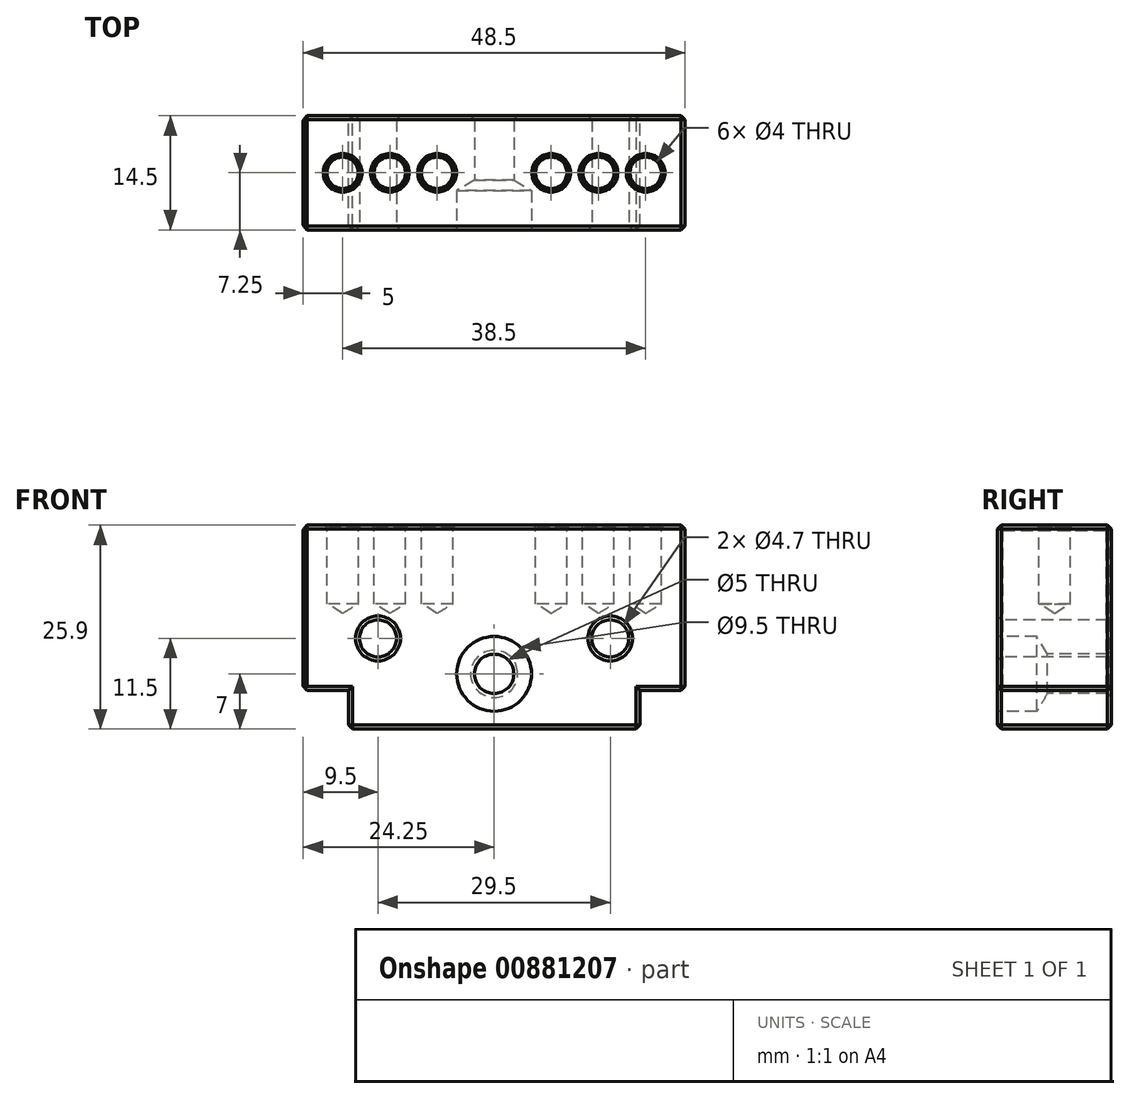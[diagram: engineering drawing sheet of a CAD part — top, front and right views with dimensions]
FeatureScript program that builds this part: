
annotation { "Feature Type Name" : "Feature", "Feature Type Description" : "" }
export const myFeature = defineFeature(function(context is Context, id is Id, definition is map)
    precondition{}
    {
        {
            var Q0;
            Q0=qCreatedBy(makeId("Front.planeOp"),FACE);
            var sketch = newSketch(context, id + "F0", { "sketchPlane" : qUnion([Q0])});
            skLineSegment(sketch, "E0", {"start": v(0, 4.9) * mm, "end": v(5.75, 4.9) * mm});
            skLineSegment(sketch, "E1", {"start": v(5.75, 4.9) * mm, "end": v(5.75, 0) * mm});
            skLineSegment(sketch, "E2", {"start": v(5.75, 0) * mm, "end": v(42.75, 0) * mm});
            skLineSegment(sketch, "E3", {"start": v(42.75, 0) * mm, "end": v(42.75, 4.9) * mm});
            skLineSegment(sketch, "E4", {"start": v(42.75, 4.9) * mm, "end": v(48.5, 4.9) * mm});
            skLineSegment(sketch, "E5", {"start": v(48.5, 4.9) * mm, "end": v(48.5, 25.9) * mm});
            skLineSegment(sketch, "E6", {"start": v(48.5, 25.9) * mm, "end": v(0, 25.9) * mm});
            skLineSegment(sketch, "E7", {"start": v(0, 25.9) * mm, "end": v(0, 4.9) * mm});
            skSolve(sketch);
        }
        {
            var Q0;
            Q0=makeQuery(id+"F0.imprint","IMPRINT",FACE,{"disambiguationData":[TD([[makeQuery(id+"F0.imprint","IMPRINT",EDGE,{"derivedFrom":sQuery(id+"F0.wireOp",EDGE,"E0")}),1.0]])]});
            extrude(context, id + "F1", {"entities" : qUnion([Q0]), "depth" : 14.5 * mm, "offsetDistance" : 25 * mm});
        }
        {
            var Q0;
            Q0=makeQuery(id+"F1.opExtrude","CAP_FACE",FACE,{"disambiguationData":[OSD([sQuery(id+"F0.wireOp",EDGE,"E0"),sQuery(id+"F0.wireOp",EDGE,"E1"),sQuery(id+"F0.wireOp",EDGE,"E2"),sQuery(id+"F0.wireOp",EDGE,"E3"),sQuery(id+"F0.wireOp",EDGE,"E4"),sQuery(id+"F0.wireOp",EDGE,"E5"),sQuery(id+"F0.wireOp",EDGE,"E6"),sQuery(id+"F0.wireOp",EDGE,"E7")])],"isStart":false});
            var sketch = newSketch(context, id + "F2", { "sketchPlane" : qUnion([Q0])});
            skPoint(sketch, "E8", {"position": v(24.25, 7) * mm});
            skPoint(sketch, "E9", {"position": v(9.5, 11.5) * mm});
            skPoint(sketch, "E10", {"position": v(39, 11.5) * mm});
            skPoint(sketch, "E11.end.orphan", {"position": v(0, 7) * mm});
            skSolve(sketch);
        }
        {
            var Q0;
            Q0=sQuery(id+"F2.wireOp",VERTEX,"E9");
            var Q1;
            Q1=sQuery(id+"F2.wireOp",VERTEX,"E10");
            var Q2;
            Q2=makeQuery(id+"F1.opExtrude","SWEPT_BODY",BODY,{"disambiguationData":[OSD([sQuery(id+"F0.wireOp",EDGE,"E0"),sQuery(id+"F0.wireOp",EDGE,"E1"),sQuery(id+"F0.wireOp",EDGE,"E2"),sQuery(id+"F0.wireOp",EDGE,"E3"),sQuery(id+"F0.wireOp",EDGE,"E4"),sQuery(id+"F0.wireOp",EDGE,"E5"),sQuery(id+"F0.wireOp",EDGE,"E6"),sQuery(id+"F0.wireOp",EDGE,"E7")])]});
            hole(context, id + "F3", {"style" : HoleStyle.SIMPLE, "endStyle" : HoleEndStyle.THROUGH, "holeDiameter" : 4.7 * mm, "majorDiameter" : 5 * mm, "isTappedThrough" : true, "tappedDepth" : 6 * mm, "tapClearance" : 3, "locations" : qUnion([Q0, Q1]), "scope" : qUnion([Q2])});
        }
        {
            var Q0;
            Q0=sQuery(id+"F2.wireOp",VERTEX,"E8");
            var Q1;
            Q1=makeQuery(id+"F1.opExtrude","SWEPT_BODY",BODY,{"disambiguationData":[OSD([sQuery(id+"F0.wireOp",EDGE,"E0"),sQuery(id+"F0.wireOp",EDGE,"E1"),sQuery(id+"F0.wireOp",EDGE,"E2"),sQuery(id+"F0.wireOp",EDGE,"E3"),sQuery(id+"F0.wireOp",EDGE,"E4"),sQuery(id+"F0.wireOp",EDGE,"E5"),sQuery(id+"F0.wireOp",EDGE,"E6"),sQuery(id+"F0.wireOp",EDGE,"E7")])]});
            hole(context, id + "F4", {"style" : HoleStyle.SIMPLE, "endStyle" : HoleEndStyle.THROUGH, "standardTappedOrClearance" : lookupTablePath({ "standard" : "ISO", "engagement" : "75%", "pitch" : "1 mm", "size" : "M6", "type" : "Tapped" }), "standardBlindInLast" : lookupTablePath({ "standard" : "ISO", "engagement" : "75%", "pitch" : "1 mm", "size" : "M6", "type" : "Tapped" }), "holeDiameter" : 5 * mm, "majorDiameter" : 6 * mm, "showTappedDepth" : true, "isTappedThrough" : true, "tappedDepth" : 6 * mm, "tapClearance" : 3, "locations" : qUnion([Q0]), "scope" : qUnion([Q1])});
        }
        {
            var Q0;
            Q0=makeQuery(id+"F1.opExtrude","SWEPT_FACE",FACE,{"disambiguationData":[OSD([sQuery(id+"F0.wireOp",EDGE,"E6")])]});
            var sketch = newSketch(context, id + "F5", { "sketchPlane" : qUnion([Q0])});
            skLineSegment(sketch, "E12", {"start": v(0, -7.25) * mm, "end": v(52.15, -7.25) * mm, "construction": true});
            skPoint(sketch, "E13", {"position": v(5, -7.25) * mm});
            skPoint(sketch, "E14", {"position": v(11, -7.25) * mm});
            skPoint(sketch, "E15", {"position": v(17, -7.25) * mm});
            skLineSegment(sketch, "E16", {"start": v(24.25, 0) * mm, "end": v(24.25, -16.26) * mm, "construction": true});
            skPoint(sketch, "E17.MirrorP", {"position": v(31.5, -7.25) * mm});
            skPoint(sketch, "E18.MirrorP", {"position": v(37.5, -7.25) * mm});
            skPoint(sketch, "E19.MirrorP", {"position": v(43.5, -7.25) * mm});
            skSolve(sketch);
        }
        {
            var Q0;
            Q0=sQuery(id+"F5.wireOp",VERTEX,"E13");
            var Q1;
            Q1=sQuery(id+"F5.wireOp",VERTEX,"E14");
            var Q2;
            Q2=sQuery(id+"F5.wireOp",VERTEX,"E15");
            var Q3;
            Q3=sQuery(id+"F5.wireOp",VERTEX,"E17.MirrorP");
            var Q4;
            Q4=sQuery(id+"F5.wireOp",VERTEX,"E18.MirrorP");
            var Q5;
            Q5=sQuery(id+"F5.wireOp",VERTEX,"E19.MirrorP");
            var Q6;
            Q6=makeQuery(id+"F1.opExtrude","SWEPT_BODY",BODY,{"disambiguationData":[OSD([sQuery(id+"F0.wireOp",EDGE,"E0"),sQuery(id+"F0.wireOp",EDGE,"E1"),sQuery(id+"F0.wireOp",EDGE,"E2"),sQuery(id+"F0.wireOp",EDGE,"E3"),sQuery(id+"F0.wireOp",EDGE,"E4"),sQuery(id+"F0.wireOp",EDGE,"E5"),sQuery(id+"F0.wireOp",EDGE,"E6"),sQuery(id+"F0.wireOp",EDGE,"E7")])]});
            hole(context, id + "F6", {"style" : HoleStyle.C_SINK, "endStyle" : HoleEndStyle.BLIND, "holeDiameter" : 4 * mm, "cSinkDiameter" : 4.5 * mm, "cSinkAngle" : 90 * degree, "majorDiameter" : 5 * mm, "holeDepth" : 10 * mm, "isTappedThrough" : true, "tappedDepth" : 6 * mm, "tapClearance" : 3, "locations" : qUnion([Q0, Q1, Q2, Q3, Q4, Q5]), "scope" : qUnion([Q6])});
        }
        {
            var Q0;
            Q0=makeQuery(id+"F1.opExtrude","SWEPT_FACE",FACE,{"disambiguationData":[OSD([sQuery(id+"F0.wireOp",EDGE,"E5")])]});
            var Q1;
            Q1=makeQuery(id+"F1.opExtrude","SWEPT_FACE",FACE,{"disambiguationData":[OSD([sQuery(id+"F0.wireOp",EDGE,"E6")])]});
            var Q2;
            Q2=makeQuery(id+"F1.opExtrude","CAP_FACE",FACE,{"disambiguationData":[OSD([sQuery(id+"F0.wireOp",EDGE,"E0"),sQuery(id+"F0.wireOp",EDGE,"E1"),sQuery(id+"F0.wireOp",EDGE,"E2"),sQuery(id+"F0.wireOp",EDGE,"E3"),sQuery(id+"F0.wireOp",EDGE,"E4"),sQuery(id+"F0.wireOp",EDGE,"E5"),sQuery(id+"F0.wireOp",EDGE,"E6"),sQuery(id+"F0.wireOp",EDGE,"E7")])],"isStart":false});
            var Q3;
            Q3=makeQuery(id+"F1.opExtrude","CAP_FACE",FACE,{"disambiguationData":[OSD([sQuery(id+"F0.wireOp",EDGE,"E0"),sQuery(id+"F0.wireOp",EDGE,"E1"),sQuery(id+"F0.wireOp",EDGE,"E2"),sQuery(id+"F0.wireOp",EDGE,"E3"),sQuery(id+"F0.wireOp",EDGE,"E4"),sQuery(id+"F0.wireOp",EDGE,"E5"),sQuery(id+"F0.wireOp",EDGE,"E6"),sQuery(id+"F0.wireOp",EDGE,"E7")])],"isStart":true});
            var Q4;
            Q4=makeQuery(id+"F1.opExtrude","SWEPT_FACE",FACE,{"disambiguationData":[OSD([sQuery(id+"F0.wireOp",EDGE,"E2")])]});
            chamfer(context, id + "F7", {"entities" : qUnion([Q0, Q1, Q2, Q3, Q4]), "width" : 0.5 * mm, "tangentPropagation" : true});
        }
        {
            var Q0;
            Q0=makeQuery(id+"F1.opExtrude","SWEPT_FACE",FACE,{"disambiguationData":[OSD([sQuery(id+"F0.wireOp",EDGE,"E7")])]});
            chamfer(context, id + "F8", {"entities" : qUnion([Q0]), "width" : 0.5 * mm, "tangentPropagation" : true});
        }
        {
            var Q0;
            Q0=sQuery(id+"F2.wireOp",VERTEX,"E8");
            var Q1;
            Q1=makeQuery(id+"F1.opExtrude","SWEPT_BODY",BODY,{"disambiguationData":[OSD([sQuery(id+"F0.wireOp",EDGE,"E0"),sQuery(id+"F0.wireOp",EDGE,"E1"),sQuery(id+"F0.wireOp",EDGE,"E2"),sQuery(id+"F0.wireOp",EDGE,"E3"),sQuery(id+"F0.wireOp",EDGE,"E4"),sQuery(id+"F0.wireOp",EDGE,"E5"),sQuery(id+"F0.wireOp",EDGE,"E6"),sQuery(id+"F0.wireOp",EDGE,"E7")])]});
            hole(context, id + "F9", {"style" : HoleStyle.SIMPLE, "endStyle" : HoleEndStyle.BLIND, "holeDiameter" : 9.5 * mm, "majorDiameter" : 5 * mm, "holeDepth" : 5 * mm, "isTappedThrough" : true, "tappedDepth" : 6 * mm, "tapClearance" : 3, "locations" : qUnion([Q0]), "scope" : qUnion([Q1])});
        }
    });
